# Revit family: HERZ-Thermostatkopf M28x1.5 7230
name_source: partatom
category: Rohrzubehör
revit_build: Autodesk Revit 2018 (Build: 20190510_1515(x64)
units: mm (PartAtom-declared; Revit-internal decimal feet)

## family parameters
Arbeitsebenenbasiert = Nein
Beim Laden mit Abzugskörper schneiden = Nein
Bemaßung runder Anschluss = Durchmesser verwenden
Gemeinsam genutzt = Nein
Immer vertikal = Nein
OmniClass-Nummer = 23.65.55.14
OmniClass-Titel = Valves for Liquid Services
Teiletyp = Normal

## types (1)
- HERZ-Thermostatkopf M28x1.5 7230
    Anwendungen = Zur Montage auf allen HERZ-Ventilen, die für thermostatischen Betrieb eingerichtet sind.
    Ausführung = Heizkörperthermostat mit Flüssigkeitsfühler (Hydrosensor)
mit Stellung „0“, Frostsicherung einstellbar, mit Begrenzung und Blockierung des Sollwertbereiches. Handradfarbe weiß.
    Bestellnummer = 1723006
    Funktionsweise = Der HERZ-Thermostat dient als Fühl- und Regelelement.
Durch die Volumsänderung der Flüssigkeitsfüllung im HERZ-Hydrosensor wird die Schubspindel des Ventils bewegt.
    H01 = 34 mm
    H02 = 17 mm
    H03 = 5.5 mm  [stored 0.0180446 ft]
    H05 = 10.5 mm  [stored 0.0344488 ft]
    H06 = 3 mm  [stored 0.00984252 ft]
    H07 = 59 mm  [stored 0.19357 ft]
    H08 = 10 mm  [stored 0.0328084 ft]
    H09 = 3.5 mm  [stored 0.0114829 ft]
    Handrad = Kunststoff, weiß
    Hersteller = HERZ Armaturen Ges.m.b.H.
    R01 = 22.4 mm  [stored 0.0734908 ft]
    R02 = 12.2 mm
    R03 = 13.2 mm  [stored 0.0433071 ft]
    R04 = 14.75 mm
    R05 = 16.35 mm  [stored 0.0536417 ft]
    R06 = 24 mm  [stored 0.0787402 ft]
    R07 = 6 mm  [stored 0.019685 ft]
    S01 = 76 mm  [stored 0.249344 ft]
    S02 = 60 mm
    Sollwerbereich = 0 - 28°C
    URL = www.herz-armaturen.at
    W01 = 135.00°
    W02 = 120.00°
    automatische Frostsicherung = bei ca. 6°C

note: [stored X ft] marks values corroborated as IEEE doubles in the binary element streams (Revit-internal decimal feet)
